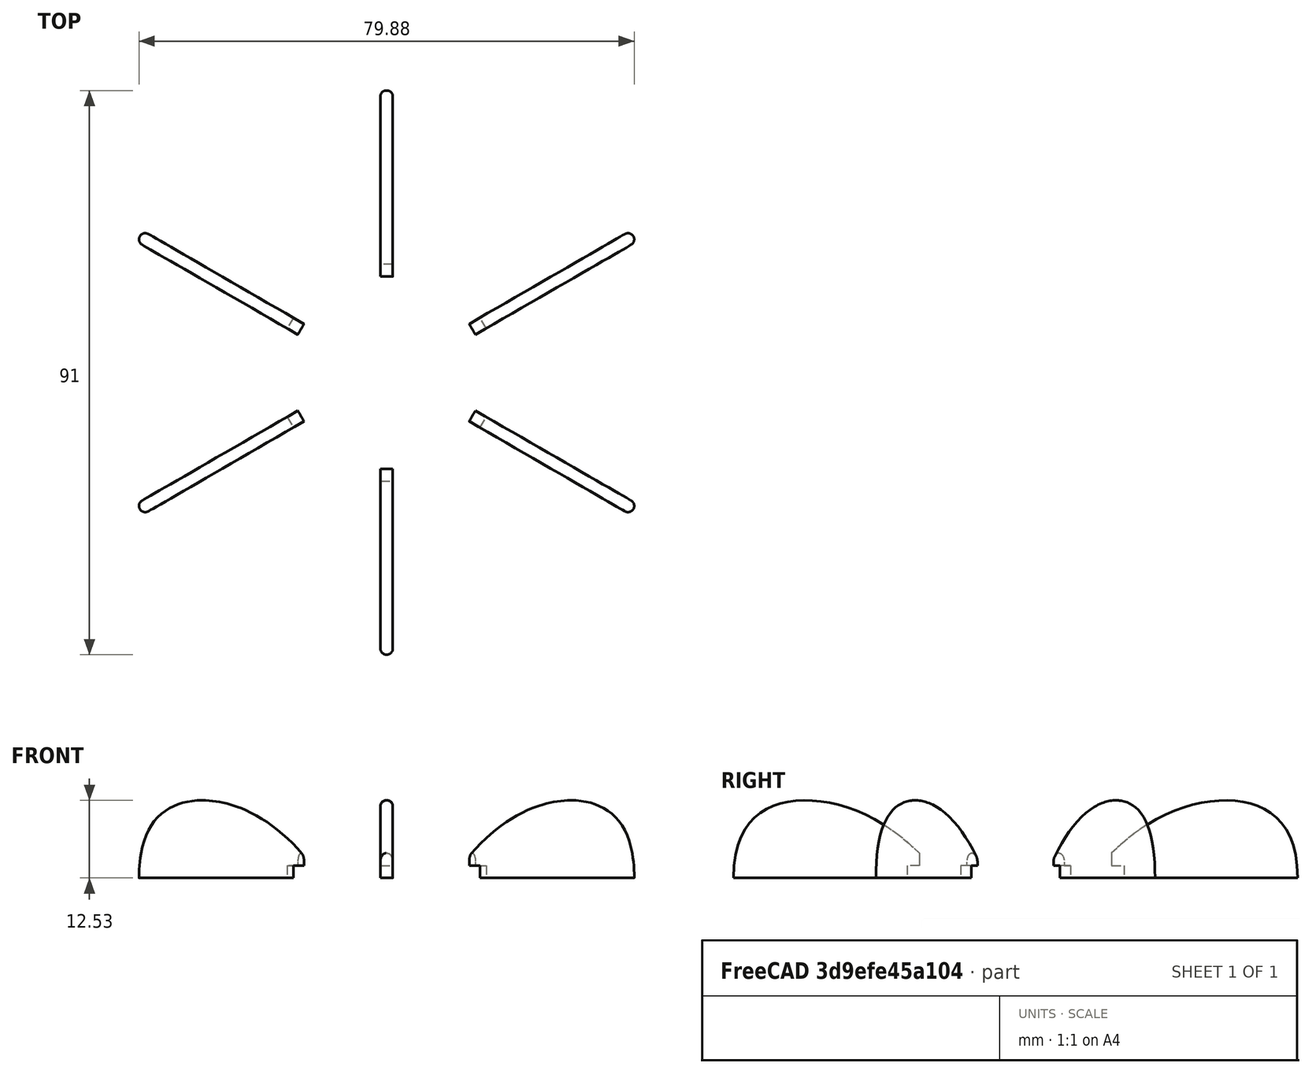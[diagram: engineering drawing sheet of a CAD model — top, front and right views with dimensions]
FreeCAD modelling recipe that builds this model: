
FCSTD DOCUMENT  (FreeCAD 0.14R3702 (Git))
Label: fan
License: CC-BY 3.0
LicenseURL: http://creativecommons.org/licenses/by/3.0/
objects: Part::Part2DObjectPython×8, Part::Feature×6, Part::Extrusion×6, PartDesign::Fillet×6, Part::Loft×2, App::DocumentObjectGroup×1
note: 28 computed .brp shape members not serialized (recipe doc carries the construction recipe); baked Part::Feature solids carry a one-line shape summary decoded from their .brp

FEATURE [Part::Part2DObjectPython] Circle  label="inner2"  # Draft 2D object (typed FeaturePython)
  FirstAngle = 0
  LastAngle = 0
  MakeFace = false
  Radius = 15.5
FEATURE [Part::Part2DObjectPython] Circle001  label="inner4"  # Draft 2D object (typed FeaturePython)
  FirstAngle = 0
  LastAngle = 0
  MakeFace = false
  Placement = pos=(0,0,17) rot=(0,0,1;0rad)
  Radius = 15.5
FEATURE [Part::Part2DObjectPython] Circle002  label="inner1"  # Draft 2D object (typed FeaturePython)
  FirstAngle = 0
  LastAngle = 0
  MakeFace = false
  Radius = 13
FEATURE [Part::Part2DObjectPython] Circle003  label="inner3"  # Draft 2D object (typed FeaturePython)
  FirstAngle = 0
  LastAngle = 0
  MakeFace = false
  Placement = pos=(0,0,17) rot=(0,0,1;0rad)
  Radius = 13
FEATURE [Part::Part2DObjectPython] Circle004  label="outer3"  # Draft 2D object (typed FeaturePython)
  FirstAngle = 0
  LastAngle = 0
  MakeFace = false
  Placement = pos=(0,0,4) rot=(0,0,1;0rad)
  Radius = 17.5
FEATURE [Part::Part2DObjectPython] Circle005  label="outer4"  # Draft 2D object (typed FeaturePython)
  FirstAngle = 0
  LastAngle = 0
  MakeFace = false
  Placement = pos=(0,0,4) rot=(0,0,1;0rad)
  Radius = 15.5
FEATURE [Part::Part2DObjectPython] Circle006  label="outer1"  # Draft 2D object (typed FeaturePython)
  FirstAngle = 0
  LastAngle = 0
  MakeFace = false
  Placement = pos=(0,0,6) rot=(0,0,1;0rad)
  Radius = 15.5
FEATURE [Part::Part2DObjectPython] Circle007  label="outer2"  # Draft 2D object (typed FeaturePython)
  FirstAngle = 0
  LastAngle = 0
  MakeFace = false
  Placement = pos=(0,0,6) rot=(0,0,1;0rad)
  Radius = 17.5
FEATURE [Part::Loft] Loft  label="inner_cylinder"
  Closed = true
  Placement = pos=(-0.0640595,0.0517067,0) rot=(0,0,1;0rad)
  Ruled = true
  Sections = -> [Circle003,Circle001,Circle,Circle002]
  Solid = false
FEATURE [Part::Loft] Loft001  label="outer_cylinder"
  Closed = false
  Ruled = true
  Sections = -> [Circle006,Circle007,Circle004,Circle005]
  Solid = false
FEATURE [Part::Feature] Face  label="right_face"
  Placement = pos=(1,0,28) rot=(0,1,0;4.71239rad)
  shape: bbox 2e-07 x 30 x 14 mm, 1 faces, 0 solids (baked)
FEATURE [Part::Extrusion] Extrude  label="blade1_extrude"
  Base = -> Face
  Dir = (-2,0,0)
  Placement = pos=(0,-4.5,0) rot=(0,0,1;0rad)
  Solid = false
FEATURE [PartDesign::Fillet] Fillet  label="blade1_fillet"
  Base = -> Extrude [Edge15,Edge14]
  Placement = pos=(0,-4.5,0) rot=(0,0,1;0rad)
  Radius = 0.9
FEATURE [Part::Feature] Face001  label="right_face001"
  Placement = pos=(1,0,28) rot=(0,-1,0;1.5708rad)
  shape: bbox 2e-07 x 30 x 14 mm, 1 faces, 0 solids (baked)
FEATURE [Part::Extrusion] Extrude001  label="blade4_extrude"
  Base = -> Face001
  Dir = (-2,0,0)
  Placement = pos=(0,4.5,0) rot=(0,0,1;3.14159rad)
  Solid = false
FEATURE [PartDesign::Fillet] Fillet001  label="blade4_fillet"
  Base = -> Extrude001 [Edge15,Edge14]
  Placement = pos=(0,4.5,0) rot=(0,0,1;3.14159rad)
  Radius = 0.99
FEATURE [Part::Feature] Face002  label="right_face002"
  Placement = pos=(1,0,28) rot=(0,-1,0;1.5708rad)
  shape: bbox 2e-07 x 30 x 14 mm, 1 faces, 0 solids (baked)
FEATURE [Part::Extrusion] Extrude002  label="blade6_extrude"
  Base = -> Face002
  Dir = (-2,0,0)
  Placement = pos=(3.5,-3,0) rot=(0,0,1;1.0472rad)
  Solid = false
FEATURE [PartDesign::Fillet] Fillet002  label="blade6_fillet"
  Base = -> Extrude002 [Edge15,Edge14]
  Placement = pos=(3.5,-3,0) rot=(0,0,1;1.0472rad)
  Radius = 0.99
FEATURE [Part::Feature] Face003  label="right_face003"
  Placement = pos=(1,0,28) rot=(0,-1,0;1.5708rad)
  shape: bbox 2e-07 x 30 x 14 mm, 1 faces, 0 solids (baked)
FEATURE [Part::Extrusion] Extrude003  label="blade5_extrude"
  Base = -> Face003
  Dir = (-2,0,0)
  Placement = pos=(3.5,3,0) rot=(0,0,1;2.0944rad)
  Solid = false
FEATURE [PartDesign::Fillet] Fillet003  label="blade5_fillet"
  Base = -> Extrude003 [Edge15,Edge14]
  Placement = pos=(3.5,3,0) rot=(0,0,1;2.0944rad)
  Radius = 0.99
FEATURE [Part::Feature] Face004  label="right_face004"
  Placement = pos=(1,0,28) rot=(0,-1,0;1.5708rad)
  shape: bbox 2e-07 x 30 x 14 mm, 1 faces, 0 solids (baked)
FEATURE [Part::Extrusion] Extrude004  label="blade2_extrude"
  Base = -> Face004
  Dir = (-2,0,0)
  Placement = pos=(-3.5,-3,0) rot=(0,0,-1;1.0472rad)
  Solid = false
FEATURE [PartDesign::Fillet] Fillet004  label="blade2_fillet"
  Base = -> Extrude004 [Edge15,Edge14]
  Placement = pos=(-3.5,-3,0) rot=(0,0,-1;1.0472rad)
  Radius = 0.99
FEATURE [Part::Feature] Face005  label="right_face005"
  Placement = pos=(1,0,28) rot=(0,-1,0;1.5708rad)
  shape: bbox 2e-07 x 30 x 14 mm, 1 faces, 0 solids (baked)
FEATURE [Part::Extrusion] Extrude005  label="blade3_extrude"
  Base = -> Face005
  Dir = (-2,0,0)
  Placement = pos=(-3.5,3,0) rot=(0,0,-1;2.0944rad)
  Solid = false
FEATURE [PartDesign::Fillet] Fillet005  label="blade3_fillet"
  Base = -> Extrude005 [Edge15,Edge14]
  Placement = pos=(-3.5,3,0) rot=(0,0,-1;2.0944rad)
  Radius = 0.99
FEATURE [App::DocumentObjectGroup] Group  label="blade"
  Group = -> [Face,Extrude,Fillet,Extrude001,Fillet001,Fillet002,Extrude002,Fillet003,Extrude003,Extrude004,Fillet004,Fillet005,Extrude005]
